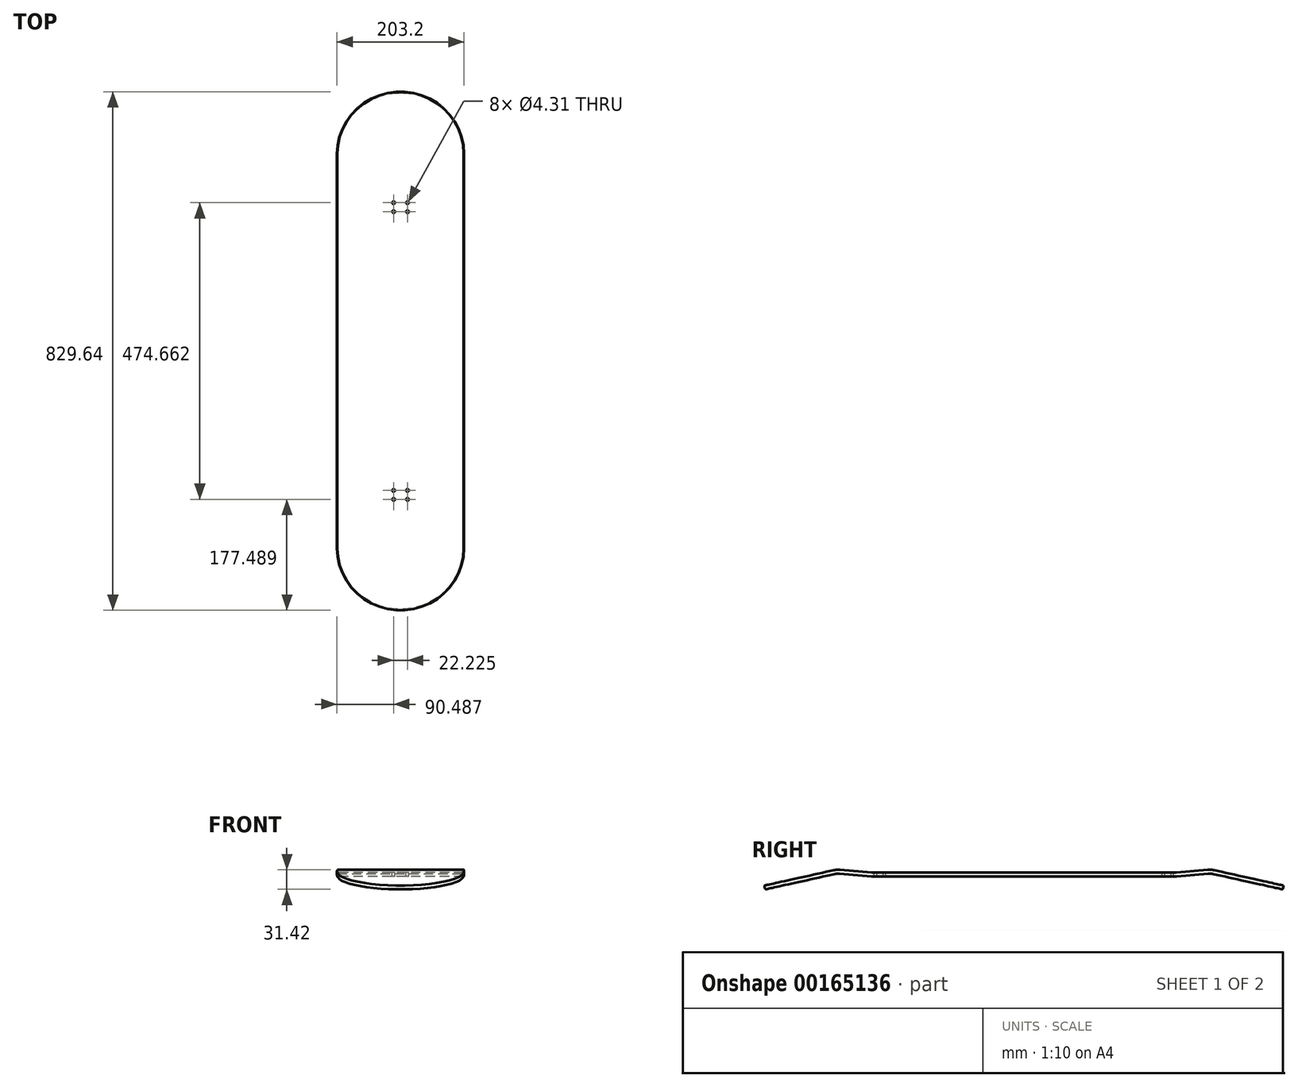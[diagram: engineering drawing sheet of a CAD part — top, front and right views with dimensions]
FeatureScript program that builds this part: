
annotation { "Feature Type Name" : "Feature", "Feature Type Description" : "" }
export const myFeature = defineFeature(function(context is Context, id is Id, definition is map)
    precondition{}
    {
        {
            var Q0;
            Q0=qCreatedBy(makeId("Top.planeOp"),FACE);
            var sketch = newSketch(context, id + "F0", { "sketchPlane" : qUnion([Q0])});
            skLineSegment(sketch, "E0.bottom", {"start": v(101.6, 241.3) * mm, "end": v(-101.6, 241.3) * mm});
            skLineSegment(sketch, "E0.top", {"start": v(101.6, -241.3) * mm, "end": v(-101.6, -241.3) * mm});
            skLineSegment(sketch, "E0.left", {"start": v(101.6, 241.3) * mm, "end": v(101.6, -241.3) * mm});
            skLineSegment(sketch, "E0.right", {"start": v(-101.6, 241.3) * mm, "end": v(-101.6, -241.3) * mm});
            skPoint(sketch, "E0.middle", {"position": v(0, 0) * mm});
            skSolve(sketch);
        }
        {
            var Q0;
            Q0=makeQuery(id+"F0.imprint","IMPRINT",FACE,{"disambiguationData":[TD([[makeQuery(id+"F0.imprint","IMPRINT",EDGE,{"derivedFrom":sQuery(id+"F0.wireOp",EDGE,"E0.bottom")}),1.0]])]});
            extrude(context, id + "F1", {"entities" : qUnion([Q0]), "depth" : 6.35 * mm});
        }
        {
            var Q0;
            Q0=makeQuery(id+"F1.opExtrude","SWEPT_FACE",FACE,{"disambiguationData":[OSD([sQuery(id+"F0.wireOp",EDGE,"E0.bottom")])]});
            var sketch = newSketch(context, id + "F2", { "sketchPlane" : qUnion([Q0])});
            skLineSegment(sketch, "E1.bottom", {"start": v(-100.8, 0) * mm, "end": v(-107.16, 0) * mm});
            skLineSegment(sketch, "E1.top", {"start": v(-100.8, 6.35) * mm, "end": v(-107.16, 6.35) * mm});
            skLineSegment(sketch, "E1.left", {"start": v(-100.8, 0) * mm, "end": v(-100.8, 6.35) * mm, "construction": true});
            skLineSegment(sketch, "E1.right", {"start": v(-107.16, 0) * mm, "end": v(-107.16, 6.35) * mm});
            skLineSegment(sketch, "E2", {"start": v(-100.8, 3.18) * mm, "end": v(-101.6, 3.18) * mm, "construction": true});
            skArc(sketch, "E3", {"start": v(-100.8, 6.35) * mm, "mid": v(-101.6, 3.17) * mm, "end": v(-100.8, 0) * mm});
            skSolve(sketch);
        }
        {
            var Q0;
            Q0=makeQuery(id+"F1.opExtrude","SWEPT_FACE",FACE,{"disambiguationData":[OSD([sQuery(id+"F0.wireOp",EDGE,"E0.left")])]});
            var sketch = newSketch(context, id + "F3", { "sketchPlane" : qUnion([Q0])});
            skLineSegment(sketch, "E4", {"start": v(241.3, 6.35) * mm, "end": v(241.3, 0) * mm});
            skArc(sketch, "E5", {"start": v(241.3, 0) * mm, "mid": v(242.68, 0.03) * mm, "end": v(244.07, 0.12) * mm});
            skArc(sketch, "E6", {"start": v(241.3, 6.35) * mm, "mid": v(242.4, 6.37) * mm, "end": v(243.51, 6.45) * mm});
            skLineSegment(sketch, "E7", {"start": v(241.3, 0) * mm, "end": v(296.89, 0) * mm, "construction": true});
            skLineSegment(sketch, "E8.bottom", {"start": v(243.51, 6.45) * mm, "end": v(294.12, 10.87) * mm});
            skLineSegment(sketch, "E8.top", {"start": v(244.07, 0.12) * mm, "end": v(294.67, 4.55) * mm});
            skLineSegment(sketch, "E8.left", {"start": v(243.51, 6.45) * mm, "end": v(244.07, 0.12) * mm, "construction": true});
            skLineSegment(sketch, "E8.right", {"start": v(294.12, 10.87) * mm, "end": v(294.67, 4.55) * mm, "construction": true});
            skLineSegment(sketch, "E9", {"start": v(241.3, 31.75) * mm, "end": v(243.51, 6.45) * mm, "construction": true});
            skArc(sketch, "E10", {"start": v(302.37, 4.05) * mm, "mid": v(298.54, 4.6) * mm, "end": v(294.67, 4.55) * mm});
            skArc(sketch, "E11", {"start": v(303.74, 10.25) * mm, "mid": v(298.95, 10.93) * mm, "end": v(294.12, 10.87) * mm});
            skLineSegment(sketch, "E12.bottom", {"start": v(302.37, 4.05) * mm, "end": v(413.98, -20.6) * mm});
            skLineSegment(sketch, "E12.top", {"start": v(303.74, 10.25) * mm, "end": v(415.35, -14.4) * mm});
            skLineSegment(sketch, "E12.left", {"start": v(302.37, 4.05) * mm, "end": v(303.74, 10.25) * mm, "construction": true});
            skLineSegment(sketch, "E12.right", {"start": v(413.98, -20.6) * mm, "end": v(415.35, -14.4) * mm});
            skLineSegment(sketch, "E13", {"start": v(296.89, 11) * mm, "end": v(415.35, 11) * mm, "construction": true});
            skLineSegment(sketch, "E14", {"start": v(415.35, 11) * mm, "end": v(415.35, -14.4) * mm, "construction": true});
            skLineSegment(sketch, "E15", {"start": v(296.89, 0) * mm, "end": v(296.89, 11) * mm, "construction": true});
            skArc(sketch, "E16", {"start": v(-244.07, 0.12) * mm, "mid": v(-242.68, 0.03) * mm, "end": v(-241.3, 0) * mm});
            skArc(sketch, "E17", {"start": v(-243.51, 6.45) * mm, "mid": v(-242.4, 6.37) * mm, "end": v(-241.3, 6.35) * mm});
            skLineSegment(sketch, "E18", {"start": v(-241.3, 0) * mm, "end": v(-241.3, 6.35) * mm});
            skLineSegment(sketch, "E19.bottom", {"start": v(-244.07, 0.12) * mm, "end": v(-294.67, 4.55) * mm});
            skLineSegment(sketch, "E19.top", {"start": v(-243.51, 6.45) * mm, "end": v(-294.12, 10.87) * mm});
            skLineSegment(sketch, "E19.left", {"start": v(-244.07, 0.12) * mm, "end": v(-243.51, 6.45) * mm, "construction": true});
            skLineSegment(sketch, "E19.right", {"start": v(-294.67, 4.55) * mm, "end": v(-294.12, 10.87) * mm, "construction": true});
            skArc(sketch, "E20", {"start": v(-294.67, 4.55) * mm, "mid": v(-298.54, 4.6) * mm, "end": v(-302.37, 4.05) * mm});
            skArc(sketch, "E21", {"start": v(-294.12, 10.87) * mm, "mid": v(-298.95, 10.93) * mm, "end": v(-303.74, 10.25) * mm});
            skLineSegment(sketch, "E22.bottom", {"start": v(-302.37, 4.05) * mm, "end": v(-413.98, -20.6) * mm});
            skLineSegment(sketch, "E22.top", {"start": v(-303.74, 10.25) * mm, "end": v(-415.35, -14.4) * mm});
            skLineSegment(sketch, "E22.left", {"start": v(-302.37, 4.05) * mm, "end": v(-303.74, 10.25) * mm, "construction": true});
            skLineSegment(sketch, "E22.right", {"start": v(-413.98, -20.6) * mm, "end": v(-415.35, -14.4) * mm});
            skLineSegment(sketch, "E23", {"start": v(294.67, 4.55) * mm, "end": v(-294.67, 4.55) * mm, "construction": true});
            skLineSegment(sketch, "E24", {"start": v(0, 6.35) * mm, "end": v(0, 4.55) * mm, "construction": true});
            skLineSegment(sketch, "E25", {"start": v(413.98, -20.6) * mm, "end": v(-413.98, -20.6) * mm, "construction": true});
            skSolve(sketch);
        }
        {
            var Q0;
            Q0=makeQuery(id+"F3.imprint","IMPRINT",FACE,{"disambiguationData":[TD([[makeQuery(id+"F3.imprint","IMPRINT",EDGE,{"derivedFrom":sQuery(id+"F3.wireOp",EDGE,"E4")}),1.0]])]});
            var Q1;
            Q1=makeQuery(id+"F3.imprint","IMPRINT",FACE,{"disambiguationData":[TD([[makeQuery(id+"F3.imprint","IMPRINT",EDGE,{"derivedFrom":sQuery(id+"F3.wireOp",EDGE,"E16")}),1.0]])]});
            var Q2;
            Q2=makeQuery(id+"F1.opExtrude","SWEPT_FACE",FACE,{"disambiguationData":[OSD([sQuery(id+"F0.wireOp",EDGE,"E0.right")])]});
            extrude(context, id + "F4", {"entities" : qUnion([Q0, Q1]), "operationType" : NewBodyOperationType.ADD, "endBound" : BoundingType.UP_TO_SURFACE, "oppositeDirection" : true, "endBoundEntityFace" : qUnion([Q2]), "depth" : 25.4 * mm});
        }
        {
            var Q0;
            Q0=makeQuery(id+"F4.opExtrude","CAP_EDGE",EDGE,{"disambiguationData":[OSD([sQuery(id+"F3.wireOp",EDGE,"E12.right")])],"isStart":true});
            var Q1;
            Q1=makeQuery(id+"F4.opExtrude","CAP_EDGE",EDGE,{"disambiguationData":[OSD([sQuery(id+"F3.wireOp",EDGE,"E12.right")])],"isStart":false});
            var Q2;
            Q2=makeQuery(id+"F4.opExtrude","CAP_EDGE",EDGE,{"disambiguationData":[OSD([sQuery(id+"F3.wireOp",EDGE,"E22.right")])],"isStart":true});
            var Q3;
            Q3=makeQuery(id+"F4.opExtrude","CAP_EDGE",EDGE,{"disambiguationData":[OSD([sQuery(id+"F3.wireOp",EDGE,"E22.right")])],"isStart":false});
            fillet(context, id + "F5", {"entities" : qUnion([Q0, Q1, Q2, Q3]), "radius" : 101.6 * mm, "tangentPropagation" : true, "allowEdgeOverflow" : false});
        }
        {
            var Q0;
            Q0 = qSketchRegion(id + "F2", true);
            var Q1;
            Q1=makeQuery(id+"F1.opExtrude","CAP_EDGE",EDGE,{"disambiguationData":[OSD([sQuery(id+"F0.wireOp",EDGE,"E0.left")])],"isStart":true});
            var Q2;
            Q2=makeQuery(id+"F4.opExtrude","CAP_EDGE",EDGE,{"disambiguationData":[OSD([sQuery(id+"F3.wireOp",EDGE,"E16")])],"isStart":true});
            var Q3;
            Q3=makeQuery(id+"F4.opExtrude","CAP_EDGE",EDGE,{"disambiguationData":[OSD([sQuery(id+"F3.wireOp",EDGE,"E19.bottom")])],"isStart":true});
            var Q4;
            Q4=makeQuery(id+"F4.opExtrude","CAP_EDGE",EDGE,{"disambiguationData":[OSD([sQuery(id+"F3.wireOp",EDGE,"E20")])],"isStart":true});
            var Q5;
            Q5=makeQuery(id+"F4.opExtrude","CAP_EDGE",EDGE,{"disambiguationData":[OSD([sQuery(id+"F3.wireOp",EDGE,"E22.bottom")])],"isStart":true});
            var Q6;
            Q6=makeQuery(id+"F5.opFillet","BLEND_EDGE",EDGE,{"blendedFrom":[makeQuery(id+"F4.opExtrude","CAP_EDGE",EDGE,{"disambiguationData":[OSD([sQuery(id+"F3.wireOp",EDGE,"E22.right")])],"isStart":true}),makeQuery(id+"F4.opExtrude","SWEPT_FACE",FACE,{"disambiguationData":[OSD([sQuery(id+"F3.wireOp",EDGE,"E22.bottom")])]})],"blendedInto":[makeQuery(id+"F4.opExtrude","SWEPT_FACE",FACE,{"disambiguationData":[OSD([sQuery(id+"F3.wireOp",EDGE,"E22.bottom")])]})]});
            var Q7;
            Q7=makeQuery(id+"F4.opExtrude","CAP_EDGE",EDGE,{"disambiguationData":[OSD([sQuery(id+"F3.wireOp",EDGE,"E22.bottom")])],"isStart":false});
            var Q8;
            Q8=makeQuery(id+"F4.opExtrude","CAP_EDGE",EDGE,{"disambiguationData":[OSD([sQuery(id+"F3.wireOp",EDGE,"E20")])],"isStart":false});
            var Q9;
            Q9=makeQuery(id+"F4.opExtrude","CAP_EDGE",EDGE,{"disambiguationData":[OSD([sQuery(id+"F3.wireOp",EDGE,"E19.bottom")])],"isStart":false});
            var Q10;
            Q10=makeQuery(id+"F4.opExtrude","CAP_EDGE",EDGE,{"disambiguationData":[OSD([sQuery(id+"F3.wireOp",EDGE,"E16")])],"isStart":false});
            var Q11;
            Q11=makeQuery(id+"F1.opExtrude","CAP_EDGE",EDGE,{"disambiguationData":[OSD([sQuery(id+"F0.wireOp",EDGE,"E0.right")])],"isStart":true});
            var Q12;
            Q12=makeQuery(id+"F4.opExtrude","CAP_EDGE",EDGE,{"disambiguationData":[OSD([sQuery(id+"F3.wireOp",EDGE,"E5")])],"isStart":false});
            var Q13;
            Q13=makeQuery(id+"F4.opExtrude","CAP_EDGE",EDGE,{"disambiguationData":[OSD([sQuery(id+"F3.wireOp",EDGE,"E8.top")])],"isStart":false});
            var Q14;
            Q14=makeQuery(id+"F4.opExtrude","CAP_EDGE",EDGE,{"disambiguationData":[OSD([sQuery(id+"F3.wireOp",EDGE,"E10")])],"isStart":false});
            var Q15;
            Q15=makeQuery(id+"F4.opExtrude","CAP_EDGE",EDGE,{"disambiguationData":[OSD([sQuery(id+"F3.wireOp",EDGE,"E12.bottom")])],"isStart":false});
            var Q16;
            Q16=makeQuery(id+"F5.opFillet","BLEND_EDGE",EDGE,{"blendedFrom":[makeQuery(id+"F4.opExtrude","CAP_EDGE",EDGE,{"disambiguationData":[OSD([sQuery(id+"F3.wireOp",EDGE,"E12.right")])],"isStart":true}),makeQuery(id+"F4.opExtrude","SWEPT_FACE",FACE,{"disambiguationData":[OSD([sQuery(id+"F3.wireOp",EDGE,"E12.bottom")])]})],"blendedInto":[makeQuery(id+"F4.opExtrude","SWEPT_FACE",FACE,{"disambiguationData":[OSD([sQuery(id+"F3.wireOp",EDGE,"E12.bottom")])]})]});
            var Q17;
            Q17=makeQuery(id+"F4.opExtrude","CAP_EDGE",EDGE,{"disambiguationData":[OSD([sQuery(id+"F3.wireOp",EDGE,"E12.bottom")])],"isStart":true});
            var Q18;
            Q18=makeQuery(id+"F4.opExtrude","CAP_EDGE",EDGE,{"disambiguationData":[OSD([sQuery(id+"F3.wireOp",EDGE,"E10")])],"isStart":true});
            var Q19;
            Q19=makeQuery(id+"F4.opExtrude","CAP_EDGE",EDGE,{"disambiguationData":[OSD([sQuery(id+"F3.wireOp",EDGE,"E8.top")])],"isStart":true});
            var Q20;
            Q20=makeQuery(id+"F4.opExtrude","CAP_EDGE",EDGE,{"disambiguationData":[OSD([sQuery(id+"F3.wireOp",EDGE,"E5")])],"isStart":true});
            sweep(context, id + "F6", {"operationType" : NewBodyOperationType.REMOVE, "profiles" : qUnion([Q0]), "path" : qUnion([Q1, Q2, Q3, Q4, Q5, Q6, Q7, Q8, Q9, Q10, Q11, Q12, Q13, Q14, Q15, Q16, Q17, Q18, Q19, Q20])});
        }
        {
            var Q0;
            Q0=makeQuery(id+"F1.opExtrude","CAP_FACE",FACE,{"disambiguationData":[OSD([sQuery(id+"F0.wireOp",EDGE,"E0.bottom"),sQuery(id+"F0.wireOp",EDGE,"E0.top"),sQuery(id+"F0.wireOp",EDGE,"E0.left"),sQuery(id+"F0.wireOp",EDGE,"E0.right")])],"isStart":false});
            var sketch = newSketch(context, id + "F7", { "sketchPlane" : qUnion([Q0])});
            skLineSegment(sketch, "E26", {"start": v(0, 241.3) * mm, "end": v(0, 237.33) * mm, "construction": true});
            skLineSegment(sketch, "E27", {"start": v(0, -241.3) * mm, "end": v(0, -237.33) * mm, "construction": true});
            skLineSegment(sketch, "E28.bottom", {"start": v(-11.11, 237.33) * mm, "end": v(11.11, 237.33) * mm, "construction": true});
            skLineSegment(sketch, "E28.top", {"start": v(-11.11, 223.04) * mm, "end": v(11.11, 223.04) * mm, "construction": true});
            skLineSegment(sketch, "E28.left", {"start": v(-11.11, 237.33) * mm, "end": v(-11.11, 223.04) * mm, "construction": true});
            skLineSegment(sketch, "E28.right", {"start": v(11.11, 237.33) * mm, "end": v(11.11, 223.04) * mm, "construction": true});
            skLineSegment(sketch, "E29.bottom", {"start": v(-11.11, -237.33) * mm, "end": v(11.11, -237.33) * mm, "construction": true});
            skLineSegment(sketch, "E29.top", {"start": v(-11.11, -223.04) * mm, "end": v(11.11, -223.04) * mm, "construction": true});
            skLineSegment(sketch, "E29.left", {"start": v(-11.11, -237.33) * mm, "end": v(-11.11, -223.04) * mm, "construction": true});
            skLineSegment(sketch, "E29.right", {"start": v(11.11, -237.33) * mm, "end": v(11.11, -223.04) * mm, "construction": true});
            skCircle(sketch, "E30", {"center": v(-11.11, 237.33) * mm, "radius": 2.15 * mm});
            skCircle(sketch, "E31", {"center": v(11.11, 237.33) * mm, "radius": 2.15 * mm});
            skCircle(sketch, "E32", {"center": v(11.11, 223.04) * mm, "radius": 2.15 * mm});
            skCircle(sketch, "E33", {"center": v(-11.11, 223.04) * mm, "radius": 2.15 * mm});
            skCircle(sketch, "E34", {"center": v(11.11, -223.04) * mm, "radius": 2.15 * mm});
            skCircle(sketch, "E35", {"center": v(-11.11, -223.04) * mm, "radius": 2.15 * mm});
            skCircle(sketch, "E36", {"center": v(-11.11, -237.33) * mm, "radius": 2.15 * mm});
            skCircle(sketch, "E37", {"center": v(11.11, -237.33) * mm, "radius": 2.15 * mm});
            skSolve(sketch);
        }
        {
            var Q0;
            Q0 = qSketchRegion(id + "F7", true);
            var Q1;
            Q1=makeQuery(id+"F1.opExtrude","CAP_FACE",FACE,{"disambiguationData":[OSD([sQuery(id+"F0.wireOp",EDGE,"E0.bottom"),sQuery(id+"F0.wireOp",EDGE,"E0.top"),sQuery(id+"F0.wireOp",EDGE,"E0.left"),sQuery(id+"F0.wireOp",EDGE,"E0.right")])],"isStart":true});
            extrude(context, id + "F8", {"entities" : qUnion([Q0]), "operationType" : NewBodyOperationType.REMOVE, "endBound" : BoundingType.UP_TO_SURFACE, "oppositeDirection" : true, "endBoundEntityFace" : qUnion([Q1]), "depth" : 25.4 * mm});
        }
    });
